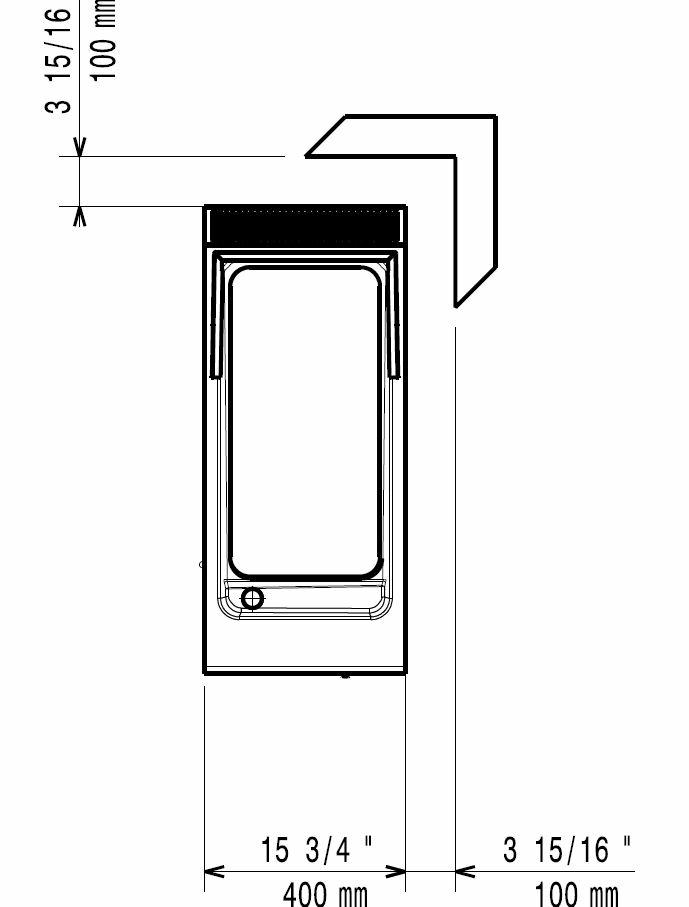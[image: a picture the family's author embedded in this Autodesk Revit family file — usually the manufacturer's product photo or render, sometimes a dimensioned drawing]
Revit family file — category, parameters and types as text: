
# Revit family: QF_ELECTROLUXPROFESSIONAL_391053_E9FTGDCS00
name_source: partatom
category: Specialty Equipment
revit_build: Autodesk Revit 2018 (Build: 20190510_1515(x64)
units: mm (PartAtom-declared; Revit-internal decimal feet)

## family parameters
Always vertical = Yes
Cut with Voids When Loaded = No
Part Type = Normal
Room Calculation Point = No
Round Connector Dimension = Use Diameter
Shared = No
Work Plane-Based = No

## types (1)
- QF_ELECTROLUXPROFESSIONAL_391053_E9FTGDCS00
    Depth = 930 mm  [stored 3.05118 ft]
    Description = 900XP HALF MODULE GAS FRY TOP, SMOOTH SLOPED PLATE, CHROMIUM PLATED
    Direct Waste Size = 0"
    Gas Connection Height = 0 mm  [stored 0 ft]
    Gas Size = 1"
    HP = 0 HP
    Height = 410 mm
    Manufacturer = ELECTROLUX
    Model = 391053
    URL = www.electrolux.com/foodservice
    URL Cutsheet = www.electrolux.com/foodservice
    Watts = 0 W
    Weight in Pounds = 55
    Width = 400 mm  [stored 1.31234 ft]

note: [stored X ft] marks values corroborated as IEEE doubles in the binary element streams (Revit-internal decimal feet)

## geometry (parser evidence)
native form markers: Blend x28, Sweep x2
no freeform markers — native parametric forms only
